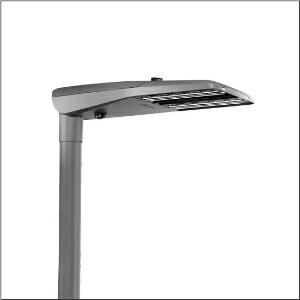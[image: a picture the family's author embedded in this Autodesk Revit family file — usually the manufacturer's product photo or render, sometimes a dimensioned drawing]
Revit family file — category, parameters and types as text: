
# Revit family: streetlight_sl_11_iq_midi___pc-l_5xc3e11y08me_a024
name_source: partatom
category: Lighting Fixtures
units: mm (PartAtom-declared; Revit-internal decimal feet)

## family parameters
Cut with Voids When Loaded = No
Host = Face
Light Source = No
Part Type = Normal
Room Calculation Point = No
Round Connector Dimension = Use Diameter
Shared = No

## types (1)
- --- (1 x LED, 9610 lm, 123.4 W, 1800K)
    Apparent Load = 123 VA
    CIE Flux Codes = 37 73 96 100 100
    Color Rendering = 70
    Color Temperature = 1800K
    Default Elevation = 1800 mm  [stored 5.90551 ft]
    Description = Streetlight SL 11 iQ midi, mast luminaire, primary light control with 3 zone facetted reflector, of plastic, silver coated, highly specular, primary optical cover: cover, of PMMA, transparent, light distribution: PC-L, light emission: direct distribution, primary light characteristic: asymmetric, left, installation type: post-top, side-entry, LED, High Power LED, rated luminous flux: 9.610lm, luminous efficacy: 78lm/W, light colour: 718, colour temperature: 1800K, control: presetting dimming logarithmic, Street-Remote, Auto-Match, Temp-Guard, Lumen-Switch, Night-Set, Smart-Wire, Light-Fading, Desk-Remote (wireless, voltage-free reading and setting of iQ features in the workshop via application-optimized NFC function/RFID function), optimised constant luminous flux control (CLO 2.0), with cable H07RN-F 5x 1.5mm², mains connection: 230..240V, AC, 50/60Hz, connection cable pre-assembled, cable length: 12,5m, start of lifetime: 123W, end of service life: 131W, reduction: 54W, luminaire housing, of diecast aluminium, powder-coated, Siteco® metallic grey (DB 702S), please order mast flange separately, inclination adjustable without tools: 0°, 5°, 10°, 15° (post-top) | 0°, -5°, -10°, -15° (side-entry), sealing non-destructively replaceable, multi-level sealing system, length: 780mm, width: 376mm, height: 118mm, mast flange for spigot size: 42mm (side-entry): 5XC10008XM4, 60/48mm (side-entry/post-top): 5XC10108XM2, 76/60mm (side-entry/post-top): 5XC10108XM1, equipment: Power, Smart Interface below and above, protection rating (complete): IP66, insulation class (complete): insulation class II (safety insulation), certification: CE, ENEC, VDE, UKCA, impact resistance: IK09, permissible operating ambient temperature for outdoor applications: -25..+50°C, standard-compliant lighting for roads and squares, Environmental Product Declaration (EPD) tested and certified by an independent institute, packaging unit: 1 piece

Light Distribution: PC-L
    Height = 118 mm
    Lamp = 1 x LED
    Lamp Light Flux = 9610 lm
    Lamp Power = 123.4 W
    Lamp count = 1
    Length = 780 mm
    Luminous efficacy = 78 lm/W
    Manufacturer = Siteco
    ModVariant = No
    Model = 5XC3E11Y08ME
    Number of Poles = 1
    OnlyDefault = Yes
    Power Factor = 1
    Product Name = Streetlight SL 11 iQ midi | PC-L
    Product group = mast luminaire | pylon top
    ProductGroupID = 6100
    Protection Class = Protection class II
    Protection Degree = IP 66
    RLX_Detail_Level = 1
    RLX_Emergency_Light_Flux = 0 lm
    RLX_Emergency_Type = 0
    RLX_Emergency_Type_DB = No
    RlxData = <blob elided: 73529 chars, md5=232f71b9>
    Socket = socket
    Standby Power = 0 W
    System Light Flux = 9610 lm
    System Power = 123 W
    Type Comments = factory setting: luminous flux: 100 % | dim-lin: 254 | 553 mA
    Type Image = l_1004429.jpg
    URL = http://relux.com
    VarID = @adj_058261
    Voltage = 0 V
    Weight = 0.00 kg
    Width = 376 mm

note: [stored X ft] marks values corroborated as IEEE doubles in the binary element streams (Revit-internal decimal feet)

## geometry (parser evidence)
native form markers: Blend x4, Sweep x12
no freeform markers — native parametric forms only
